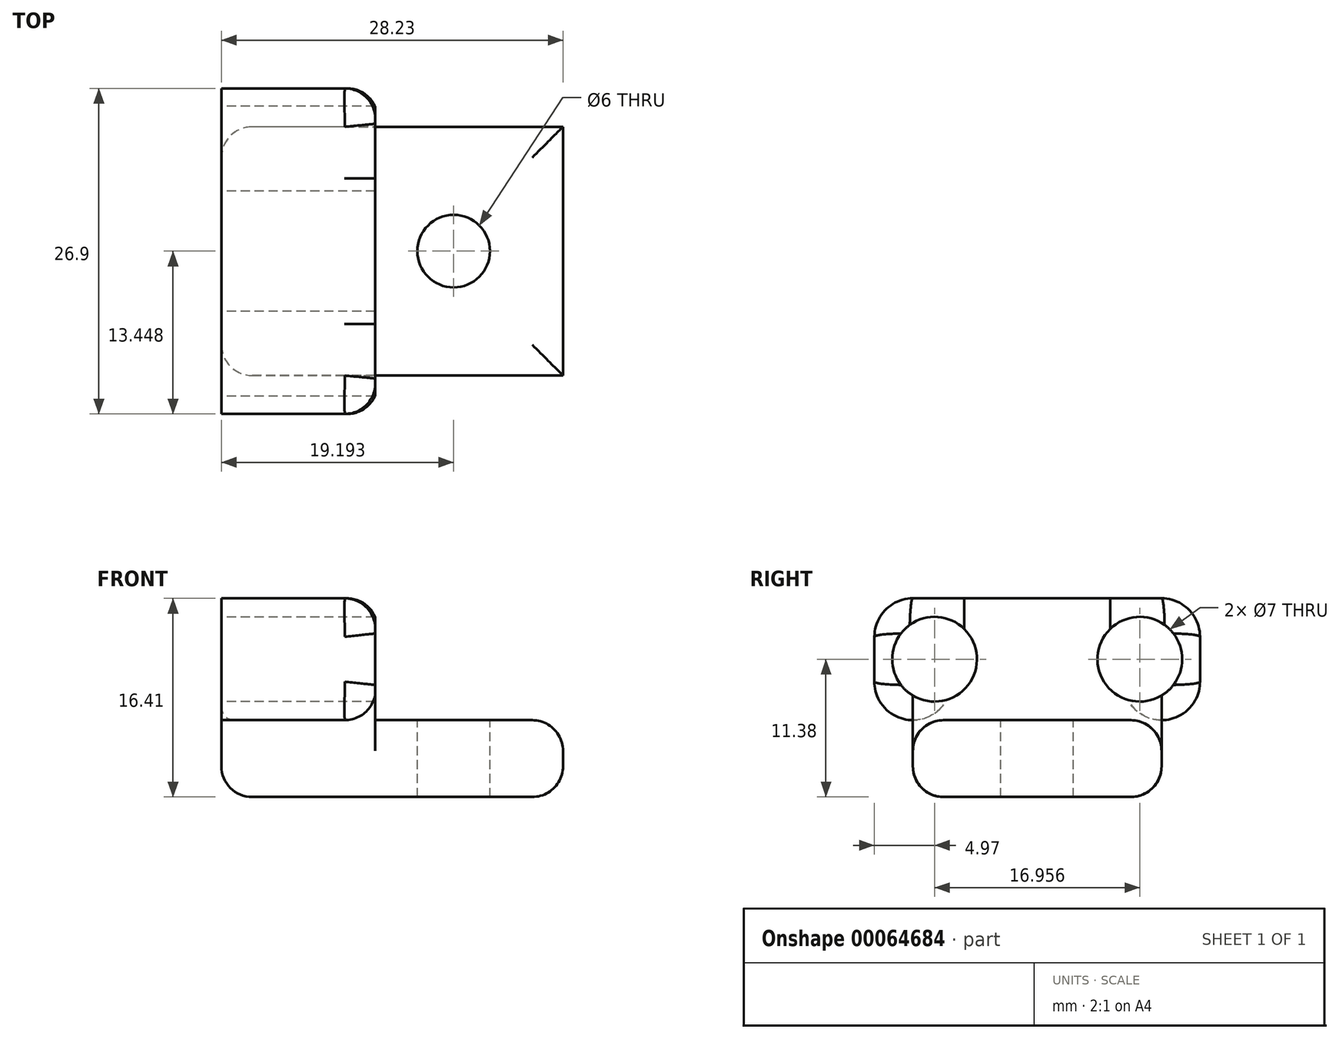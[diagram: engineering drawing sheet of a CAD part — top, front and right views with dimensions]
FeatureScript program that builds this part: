
annotation { "Feature Type Name" : "Feature", "Feature Type Description" : "" }
export const myFeature = defineFeature(function(context is Context, id is Id, definition is map)
    precondition{}
    {
        {
            var Q0;
            Q0=qCreatedBy(makeId("Right.planeOp"),FACE);
            var sketch = newSketch(context, id + "F0", { "sketchPlane" : qUnion([Q0])});
            skCircle(sketch, "E0", {"center": v(0, 0) * mm, "radius": 7 * mm});
            skCircle(sketch, "E1", {"center": v(33.91, 0) * mm, "radius": 7 * mm});
            skLineSegment(sketch, "E2.rect.bottom", {"start": v(37.51, -10.07) * mm, "end": v(-3.6, -10.07) * mm});
            skLineSegment(sketch, "E2.rect.top", {"start": v(37.51, 10.07) * mm, "end": v(-3.6, 10.07) * mm});
            skLineSegment(sketch, "E2.rect.left", {"start": v(43.86, -3.72) * mm, "end": v(43.86, 3.72) * mm});
            skLineSegment(sketch, "E2.rect.right", {"start": v(-9.95, -3.72) * mm, "end": v(-9.95, 3.72) * mm});
            skArc(sketch, "E3.filletArc", {"start": v(-3.6, 10.07) * mm, "mid": v(-8.09, 8.2) * mm, "end": v(-9.95, 3.72) * mm});
            skArc(sketch, "E4.filletArc", {"start": v(-9.95, -3.72) * mm, "mid": v(-8.09, -8.2) * mm, "end": v(-3.6, -10.07) * mm});
            skArc(sketch, "E5.filletArc", {"start": v(37.51, -10.07) * mm, "mid": v(42, -8.2) * mm, "end": v(43.86, -3.72) * mm});
            skArc(sketch, "E6.filletArc", {"start": v(43.86, 3.72) * mm, "mid": v(42, 8.2) * mm, "end": v(37.51, 10.07) * mm});
            skSolve(sketch);
        }
        {
            var Q0;
            Q0 = qSketchRegion(id + "F0", true);
            extrude(context, id + "F1", {"entities" : qUnion([Q0]), "depth" : 12.7 * mm});
        }
        {
            var Q0;
            Q0=makeQuery(id+"F1.opExtrude","SWEPT_FACE",FACE,{"disambiguationData":[OSD([sQuery(id+"F0.wireOp",EDGE,"E2.rect.bottom")])]});
            var sketch = newSketch(context, id + "F2", { "sketchPlane" : qUnion([Q0])});
            skLineSegment(sketch, "E7", {"start": v(12.7, 3.6) * mm, "end": v(43.75, 3.6) * mm});
            skLineSegment(sketch, "E8", {"start": v(43.75, 3.6) * mm, "end": v(43.75, -37.51) * mm});
            skLineSegment(sketch, "E9", {"start": v(43.75, -37.51) * mm, "end": v(12.7, -37.51) * mm});
            skSolve(sketch);
        }
        {
            var Q0;
            Q0=makeQuery(id+"F2.imprint","IMPRINT",FACE,{"disambiguationData":[TD([[makeQuery(id+"F2.imprint","IMPRINT",EDGE,{"derivedFrom":sQuery(id+"F2.wireOp",EDGE,"E7")}),-1.0]])]});
            var Q1;
            {var subQ0=sQuery(id+"F0.wireOp",EDGE,"E2.rect.bottom");Q1=makeQuery(id+"F2.imprint","IMPRINT",FACE,{"disambiguationData":[TD([[makeQuery(id+"F2.imprint","IMPRINT",EDGE,{"derivedFrom":makeQuery(id+"F1.opExtrude","CAP_EDGE",EDGE,{"disambiguationData":[OSD([subQ0])],"isStart":true})}),-1.0]])]});}
            extrude(context, id + "F3", {"entities" : qUnion([Q0, Q1]), "operationType" : NewBodyOperationType.ADD, "depth" : 12.7 * mm});
        }
        {
            var Q0;
            Q0=makeQuery(id+"F3.opExtrude","CAP_FACE",FACE,{"disambiguationData":[OSD([sQuery(id+"F0.wireOp",EDGE,"E2.rect.bottom"),sQuery(id+"F0.wireOp",EDGE,"E4.filletArc"),sQuery(id+"F0.wireOp",EDGE,"E5.filletArc"),sQuery(id+"F2.wireOp",EDGE,"E7"),sQuery(id+"F2.wireOp",EDGE,"E8"),sQuery(id+"F2.wireOp",EDGE,"E9")])],"isStart":true});
            var sketch = newSketch(context, id + "F4", { "sketchPlane" : qUnion([Q0])});
            skCircle(sketch, "E10", {"center": v(25.69, 16.96) * mm, "radius": 6 * mm});
            skSolve(sketch);
        }
        {
            var Q0;
            Q0 = qSketchRegion(id + "F4", true);
            extrude(context, id + "F5", {"entities" : qUnion([Q0]), "operationType" : NewBodyOperationType.REMOVE, "oppositeDirection" : true, "depth" : 25.4 * mm});
        }
        {
            var Q0;
            {var subQ0=sQuery(id+"F0.wireOp",EDGE,"E2.rect.bottom");Q0=makeQuery(id+"F3.boolean.opBoolean","MERGE",FACE,{"derivedFrom":[makeQuery(id+"F1.opExtrude","CAP_FACE",FACE,{"disambiguationData":[OSD([sQuery(id+"F0.wireOp",EDGE,"E0"),sQuery(id+"F0.wireOp",EDGE,"E1"),subQ0,sQuery(id+"F0.wireOp",EDGE,"E2.rect.top"),sQuery(id+"F0.wireOp",EDGE,"E2.rect.left"),sQuery(id+"F0.wireOp",EDGE,"E2.rect.right"),sQuery(id+"F0.wireOp",EDGE,"E3.filletArc"),sQuery(id+"F0.wireOp",EDGE,"E4.filletArc"),sQuery(id+"F0.wireOp",EDGE,"E5.filletArc"),sQuery(id+"F0.wireOp",EDGE,"E6.filletArc")])],"isStart":true}),makeQuery(id+"F3.opExtrude","SWEPT_FACE",FACE,{"disambiguationData":[OSD([subQ0])]})]});}
            extrude(context, id + "F6", {"entities" : qUnion([Q0]), "operationType" : NewBodyOperationType.ADD, "depth" : 12.7 * mm});
        }
        {
            var Q0;
            Q0=makeQuery(id+"F1.opExtrude","CAP_EDGE",EDGE,{"disambiguationData":[OSD([sQuery(id+"F0.wireOp",EDGE,"E2.rect.top")])],"isStart":false});
            fillet(context, id + "F7", {"entities" : qUnion([Q0]), "radius" : 5.08 * mm, "tangentPropagation" : true, "allowEdgeOverflow" : false});
        }
        {
            var Q0;
            Q0=makeQuery(id+"F3.boolean.opBoolean","SPLIT",EDGE,{"derivedFrom":makeQuery(id+"F3.opExtrude","CAP_EDGE",EDGE,{"disambiguationData":[OSD([sQuery(id+"F0.wireOp",EDGE,"E2.rect.bottom"),sQuery(id+"F0.wireOp",EDGE,"E4.filletArc"),sQuery(id+"F2.wireOp",EDGE,"E7")])],"isStart":true})});
            var Q1;
            Q1=makeQuery(id+"F3.opExtrude","CAP_EDGE",EDGE,{"disambiguationData":[OSD([sQuery(id+"F2.wireOp",EDGE,"E8")])],"isStart":true});
            var Q2;
            Q2=makeQuery(id+"F3.boolean.opBoolean","SPLIT",EDGE,{"derivedFrom":makeQuery(id+"F3.opExtrude","CAP_EDGE",EDGE,{"disambiguationData":[OSD([sQuery(id+"F0.wireOp",EDGE,"E2.rect.bottom"),sQuery(id+"F0.wireOp",EDGE,"E5.filletArc"),sQuery(id+"F2.wireOp",EDGE,"E9")])],"isStart":true})});
            var Q3;
            Q3=makeQuery(id+"F6.opExtrude","CAP_EDGE",EDGE,{"disambiguationData":[OSD([sQuery(id+"F0.wireOp",EDGE,"E2.rect.bottom"),sQuery(id+"F0.wireOp",EDGE,"E4.filletArc")])],"isStart":false});
            var Q4;
            Q4=makeQuery(id+"F6.opExtrude","CAP_EDGE",EDGE,{"disambiguationData":[OSD([sQuery(id+"F0.wireOp",EDGE,"E2.rect.bottom")])],"isStart":false});
            var Q5;
            Q5=makeQuery(id+"F6.opExtrude","CAP_EDGE",EDGE,{"disambiguationData":[OSD([sQuery(id+"F0.wireOp",EDGE,"E2.rect.bottom"),sQuery(id+"F0.wireOp",EDGE,"E5.filletArc")])],"isStart":false});
            var Q6;
            Q6=makeQuery(id+"F3.opExtrude","CAP_EDGE",EDGE,{"disambiguationData":[OSD([sQuery(id+"F2.wireOp",EDGE,"E8")])],"isStart":false});
            var Q7;
            {var subQ0=sQuery(id+"F0.wireOp",EDGE,"E4.filletArc");var subQ1=sQuery(id+"F0.wireOp",EDGE,"E2.rect.bottom");Q7=makeQuery(id+"F6.boolean.opBoolean","MERGE",EDGE,{"derivedFrom":[makeQuery(id+"F3.opExtrude","CAP_EDGE",EDGE,{"disambiguationData":[OSD([subQ1,subQ0,sQuery(id+"F2.wireOp",EDGE,"E7")])],"isStart":false}),makeQuery(id+"F6.opExtrude","SWEPT_EDGE",EDGE,{"disambiguationData":[OSD([subQ1,subQ0]),TDD([makeQuery(id+"F3.opExtrude","CAP_VERTEX",VERTEX,{"disambiguationData":[OSD([subQ1,subQ0])],"isStart":false})])]})]});}
            var Q8;
            {var subQ0=sQuery(id+"F0.wireOp",EDGE,"E5.filletArc");var subQ1=sQuery(id+"F0.wireOp",EDGE,"E2.rect.bottom");Q8=makeQuery(id+"F6.boolean.opBoolean","MERGE",EDGE,{"derivedFrom":[makeQuery(id+"F3.opExtrude","CAP_EDGE",EDGE,{"disambiguationData":[OSD([subQ1,subQ0,sQuery(id+"F2.wireOp",EDGE,"E9")])],"isStart":false}),makeQuery(id+"F6.opExtrude","SWEPT_EDGE",EDGE,{"disambiguationData":[OSD([subQ1,subQ0]),TDD([makeQuery(id+"F3.opExtrude","CAP_VERTEX",VERTEX,{"disambiguationData":[OSD([subQ1,subQ0])],"isStart":false})])]})]});}
            fillet(context, id + "F8", {"entities" : qUnion([Q0, Q1, Q2, Q3, Q4, Q5, Q6, Q7, Q8]), "radius" : 5.08 * mm, "tangentPropagation" : true, "allowEdgeOverflow" : false});
        }
        {
            var Q0;
            Q0=makeQuery(id+"F1.opExtrude","SWEPT_BODY",BODY,{"disambiguationData":[OSD([sQuery(id+"F0.wireOp",EDGE,"E0"),sQuery(id+"F0.wireOp",EDGE,"E1"),sQuery(id+"F0.wireOp",EDGE,"E2.rect.bottom"),sQuery(id+"F0.wireOp",EDGE,"E2.rect.top"),sQuery(id+"F0.wireOp",EDGE,"E2.rect.left"),sQuery(id+"F0.wireOp",EDGE,"E2.rect.right"),sQuery(id+"F0.wireOp",EDGE,"E3.filletArc"),sQuery(id+"F0.wireOp",EDGE,"E4.filletArc"),sQuery(id+"F0.wireOp",EDGE,"E5.filletArc"),sQuery(id+"F0.wireOp",EDGE,"E6.filletArc")])]});
            var Q1;
            Q1=qCreatedBy(makeId("Origin.pointOp"),VERTEX);
            transform(context, id + "F9", {"entities" : qUnion([Q0]), "transformType" : TransformType.SCALE_UNIFORMLY, "scale" : .5, "scalePoint" : qUnion([Q1]), "makeCopy" : false});
        }
    });
